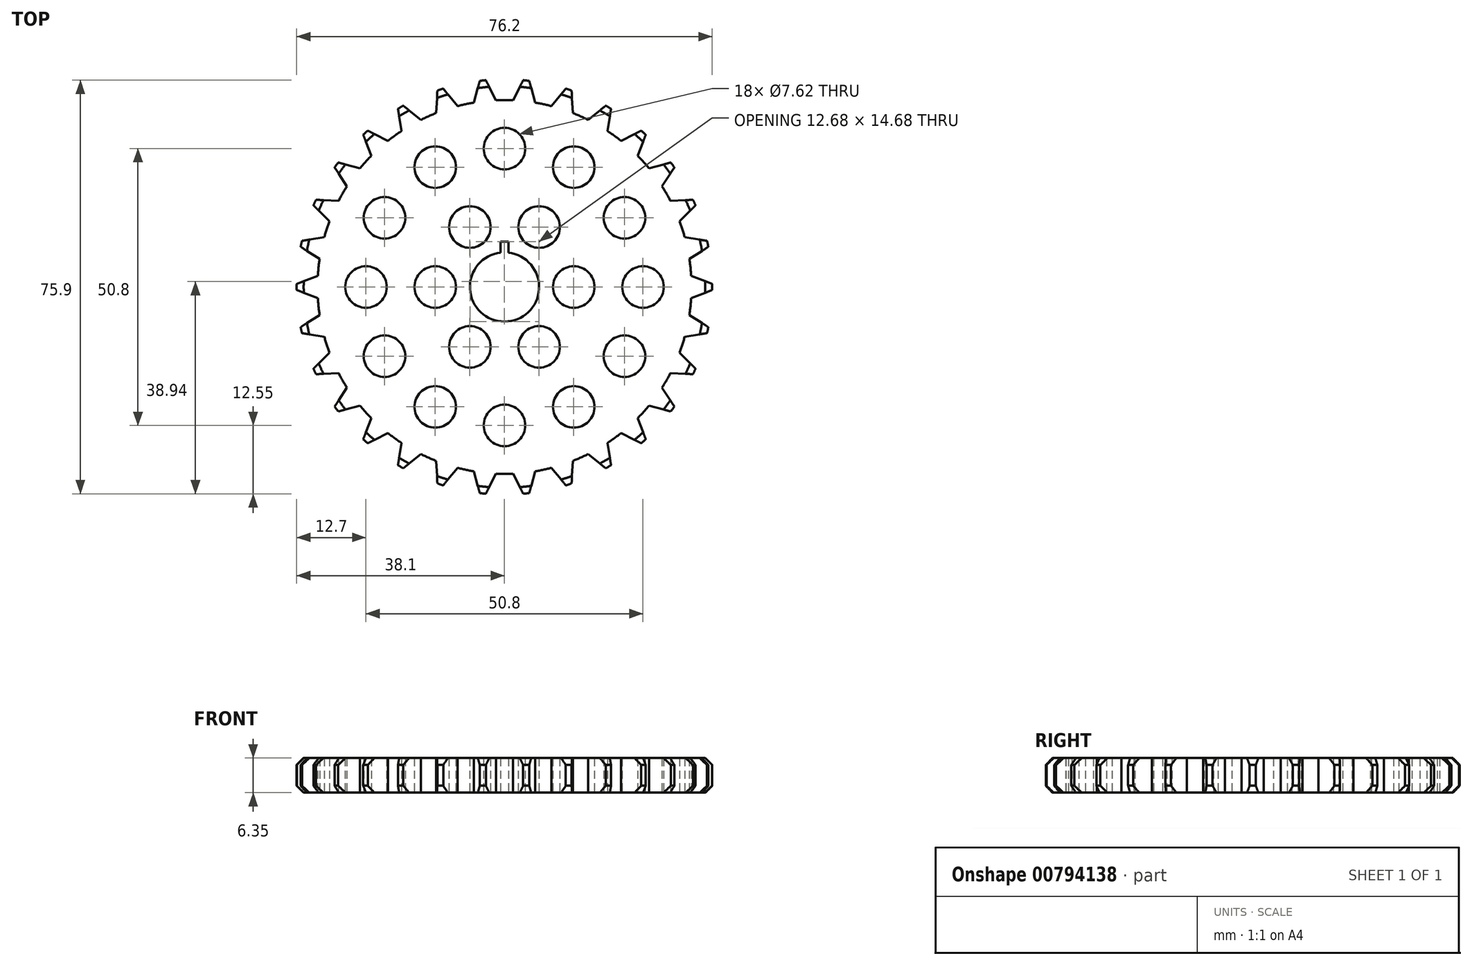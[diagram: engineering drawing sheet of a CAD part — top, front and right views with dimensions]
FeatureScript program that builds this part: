
annotation { "Feature Type Name" : "Feature", "Feature Type Description" : "" }
export const myFeature = defineFeature(function(context is Context, id is Id, definition is map)
    precondition{}
    {
        {
            var Q0;
            Q0=qCreatedBy(makeId("Top.planeOp"),FACE);
            var sketch = newSketch(context, id + "F0", { "sketchPlane" : qUnion([Q0])});
            skArc(sketch, "E0", {"start": v(12.3, 36.06) * mm, "mid": v(11.77, 36.24) * mm, "end": v(11.24, 36.4) * mm});
            skArc(sketch, "E1", {"start": v(-0.7, 6.31) * mm, "mid": v(0, -6.35) * mm, "end": v(0.7, 6.31) * mm});
            skArc(sketch, "E2", {"start": v(1.55, 34.26) * mm, "mid": v(0, 34.3) * mm, "end": v(-1.55, 34.26) * mm});
            skLineSegment(sketch, "E3", {"start": v(-1.55, 34.26) * mm, "end": v(-3.42, 37.95) * mm});
            skLineSegment(sketch, "E4.MirrorCS", {"start": v(1.55, 34.26) * mm, "end": v(3.42, 37.95) * mm});
            skArc(sketch, "E5.1.0", {"start": v(-5.61, 33.83) * mm, "mid": v(-7.13, 33.54) * mm, "end": v(-8.63, 33.19) * mm});
            skLineSegment(sketch, "E5.1.1", {"start": v(-8.63, 33.19) * mm, "end": v(-11.24, 36.4) * mm});
            skLineSegment(sketch, "E5.1.2", {"start": v(-5.61, 33.83) * mm, "end": v(-4.54, 37.83) * mm});
            skArc(sketch, "E5.2.0", {"start": v(-12.52, 31.92) * mm, "mid": v(-13.95, 31.33) * mm, "end": v(-15.34, 30.66) * mm});
            skLineSegment(sketch, "E5.2.1", {"start": v(-15.34, 30.66) * mm, "end": v(-18.56, 33.27) * mm});
            skLineSegment(sketch, "E5.2.2", {"start": v(-12.52, 31.92) * mm, "end": v(-12.3, 36.06) * mm});
            skArc(sketch, "E5.3.0", {"start": v(-18.88, 28.62) * mm, "mid": v(-20.16, 27.74) * mm, "end": v(-21.39, 26.8) * mm});
            skLineSegment(sketch, "E5.3.1", {"start": v(-21.39, 26.8) * mm, "end": v(-25.07, 28.69) * mm});
            skLineSegment(sketch, "E5.3.2", {"start": v(-18.88, 28.62) * mm, "end": v(-19.53, 32.71) * mm});
            skArc(sketch, "E5.4.0", {"start": v(-24.42, 24.07) * mm, "mid": v(-25.48, 22.94) * mm, "end": v(-26.5, 21.77) * mm});
            skLineSegment(sketch, "E5.4.1", {"start": v(-26.5, 21.77) * mm, "end": v(-30.5, 22.85) * mm});
            skLineSegment(sketch, "E5.4.2", {"start": v(-24.42, 24.07) * mm, "end": v(-25.9, 27.94) * mm});
            skArc(sketch, "E5.5.0", {"start": v(-28.9, 18.47) * mm, "mid": v(-29.7, 17.15) * mm, "end": v(-30.44, 15.79) * mm});
            skLineSegment(sketch, "E5.5.1", {"start": v(-30.44, 15.79) * mm, "end": v(-34.57, 16) * mm});
            skLineSegment(sketch, "E5.5.2", {"start": v(-28.9, 18.47) * mm, "end": v(-31.15, 21.94) * mm});
            skArc(sketch, "E5.6.0", {"start": v(-32.1, 12.06) * mm, "mid": v(-32.61, 10.6) * mm, "end": v(-33.06, 9.12) * mm});
            skLineSegment(sketch, "E5.6.1", {"start": v(-33.06, 9.12) * mm, "end": v(-37.15, 8.47) * mm});
            skLineSegment(sketch, "E5.6.2", {"start": v(-32.1, 12.06) * mm, "end": v(-35.03, 14.98) * mm});
            skArc(sketch, "E5.7.0", {"start": v(-33.9, 5.12) * mm, "mid": v(-34.1, 3.58) * mm, "end": v(-34.23, 2.04) * mm});
            skLineSegment(sketch, "E5.7.1", {"start": v(-34.23, 2.04) * mm, "end": v(-38.1, 0.56) * mm});
            skLineSegment(sketch, "E5.7.2", {"start": v(-33.9, 5.12) * mm, "end": v(-37.38, 7.37) * mm});
            skArc(sketch, "E5.8.0", {"start": v(-34.23, -2.04) * mm, "mid": v(-34.1, -3.58) * mm, "end": v(-33.9, -5.12) * mm});
            skLineSegment(sketch, "E5.8.1", {"start": v(-33.9, -5.12) * mm, "end": v(-37.38, -7.37) * mm});
            skLineSegment(sketch, "E5.8.2", {"start": v(-34.23, -2.04) * mm, "end": v(-38.1, -0.56) * mm});
            skArc(sketch, "E5.9.0", {"start": v(-33.06, -9.12) * mm, "mid": v(-32.61, -10.6) * mm, "end": v(-32.1, -12.06) * mm});
            skLineSegment(sketch, "E5.9.1", {"start": v(-32.1, -12.06) * mm, "end": v(-35.03, -14.98) * mm});
            skLineSegment(sketch, "E5.9.2", {"start": v(-33.06, -9.12) * mm, "end": v(-37.15, -8.47) * mm});
            skArc(sketch, "E5.10.0", {"start": v(-30.44, -15.79) * mm, "mid": v(-29.7, -17.14) * mm, "end": v(-28.9, -18.47) * mm});
            skLineSegment(sketch, "E5.10.1", {"start": v(-28.9, -18.47) * mm, "end": v(-31.15, -21.94) * mm});
            skLineSegment(sketch, "E5.10.2", {"start": v(-30.44, -15.79) * mm, "end": v(-34.57, -16) * mm});
            skArc(sketch, "E5.11.0", {"start": v(-26.5, -21.77) * mm, "mid": v(-25.48, -22.94) * mm, "end": v(-24.42, -24.07) * mm});
            skLineSegment(sketch, "E5.11.1", {"start": v(-24.42, -24.07) * mm, "end": v(-25.9, -27.94) * mm});
            skLineSegment(sketch, "E5.11.2", {"start": v(-26.5, -21.77) * mm, "end": v(-30.5, -22.85) * mm});
            skArc(sketch, "E5.12.0", {"start": v(-21.39, -26.8) * mm, "mid": v(-20.16, -27.74) * mm, "end": v(-18.88, -28.62) * mm});
            skLineSegment(sketch, "E5.12.1", {"start": v(-18.88, -28.62) * mm, "end": v(-19.53, -32.71) * mm});
            skLineSegment(sketch, "E5.12.2", {"start": v(-21.39, -26.8) * mm, "end": v(-25.07, -28.69) * mm});
            skArc(sketch, "E5.13.0", {"start": v(-15.34, -30.66) * mm, "mid": v(-13.95, -31.33) * mm, "end": v(-12.52, -31.92) * mm});
            skLineSegment(sketch, "E5.13.1", {"start": v(-12.52, -31.92) * mm, "end": v(-12.3, -36.06) * mm});
            skLineSegment(sketch, "E5.13.2", {"start": v(-15.34, -30.66) * mm, "end": v(-18.56, -33.27) * mm});
            skArc(sketch, "E5.14.0", {"start": v(-8.63, -33.19) * mm, "mid": v(-7.13, -33.54) * mm, "end": v(-5.61, -33.83) * mm});
            skLineSegment(sketch, "E5.14.1", {"start": v(-5.61, -33.83) * mm, "end": v(-4.54, -37.83) * mm});
            skLineSegment(sketch, "E5.14.2", {"start": v(-8.63, -33.19) * mm, "end": v(-11.24, -36.4) * mm});
            skArc(sketch, "E5.15.0", {"start": v(-1.55, -34.26) * mm, "mid": v(0, -34.3) * mm, "end": v(1.55, -34.26) * mm});
            skLineSegment(sketch, "E5.15.1", {"start": v(1.55, -34.26) * mm, "end": v(3.42, -37.95) * mm});
            skLineSegment(sketch, "E5.15.2", {"start": v(-1.55, -34.26) * mm, "end": v(-3.42, -37.95) * mm});
            skArc(sketch, "E5.16.0", {"start": v(5.61, -33.83) * mm, "mid": v(7.13, -33.54) * mm, "end": v(8.63, -33.19) * mm});
            skLineSegment(sketch, "E5.16.1", {"start": v(8.63, -33.19) * mm, "end": v(11.24, -36.4) * mm});
            skLineSegment(sketch, "E5.16.2", {"start": v(5.61, -33.83) * mm, "end": v(4.54, -37.83) * mm});
            skArc(sketch, "E5.17.0", {"start": v(12.52, -31.92) * mm, "mid": v(13.95, -31.33) * mm, "end": v(15.34, -30.66) * mm});
            skLineSegment(sketch, "E5.17.1", {"start": v(15.34, -30.66) * mm, "end": v(18.56, -33.27) * mm});
            skLineSegment(sketch, "E5.17.2", {"start": v(12.52, -31.92) * mm, "end": v(12.3, -36.06) * mm});
            skArc(sketch, "E5.18.0", {"start": v(18.88, -28.62) * mm, "mid": v(20.16, -27.74) * mm, "end": v(21.39, -26.8) * mm});
            skLineSegment(sketch, "E5.18.1", {"start": v(21.39, -26.8) * mm, "end": v(25.07, -28.69) * mm});
            skLineSegment(sketch, "E5.18.2", {"start": v(18.88, -28.62) * mm, "end": v(19.53, -32.71) * mm});
            skArc(sketch, "E5.19.0", {"start": v(24.42, -24.07) * mm, "mid": v(25.48, -22.94) * mm, "end": v(26.5, -21.77) * mm});
            skLineSegment(sketch, "E5.19.1", {"start": v(26.5, -21.77) * mm, "end": v(30.5, -22.85) * mm});
            skLineSegment(sketch, "E5.19.2", {"start": v(24.42, -24.07) * mm, "end": v(25.9, -27.94) * mm});
            skArc(sketch, "E5.20.0", {"start": v(28.9, -18.47) * mm, "mid": v(29.7, -17.15) * mm, "end": v(30.44, -15.79) * mm});
            skLineSegment(sketch, "E5.20.1", {"start": v(30.44, -15.79) * mm, "end": v(34.57, -16) * mm});
            skLineSegment(sketch, "E5.20.2", {"start": v(28.9, -18.47) * mm, "end": v(31.15, -21.94) * mm});
            skArc(sketch, "E5.21.0", {"start": v(32.1, -12.06) * mm, "mid": v(32.61, -10.6) * mm, "end": v(33.06, -9.12) * mm});
            skLineSegment(sketch, "E5.21.1", {"start": v(33.06, -9.12) * mm, "end": v(37.15, -8.47) * mm});
            skLineSegment(sketch, "E5.21.2", {"start": v(32.1, -12.06) * mm, "end": v(35.03, -14.98) * mm});
            skArc(sketch, "E5.22.0", {"start": v(33.9, -5.12) * mm, "mid": v(34.1, -3.58) * mm, "end": v(34.23, -2.04) * mm});
            skLineSegment(sketch, "E5.22.1", {"start": v(34.23, -2.04) * mm, "end": v(38.1, -0.56) * mm});
            skLineSegment(sketch, "E5.22.2", {"start": v(33.9, -5.12) * mm, "end": v(37.38, -7.37) * mm});
            skArc(sketch, "E5.23.0", {"start": v(34.23, 2.04) * mm, "mid": v(34.1, 3.58) * mm, "end": v(33.9, 5.12) * mm});
            skLineSegment(sketch, "E5.23.1", {"start": v(33.9, 5.12) * mm, "end": v(37.38, 7.37) * mm});
            skLineSegment(sketch, "E5.23.2", {"start": v(34.23, 2.04) * mm, "end": v(38.1, 0.56) * mm});
            skArc(sketch, "E5.24.0", {"start": v(33.06, 9.12) * mm, "mid": v(32.61, 10.6) * mm, "end": v(32.1, 12.06) * mm});
            skLineSegment(sketch, "E5.24.1", {"start": v(32.1, 12.06) * mm, "end": v(35.03, 14.98) * mm});
            skLineSegment(sketch, "E5.24.2", {"start": v(33.06, 9.12) * mm, "end": v(37.15, 8.47) * mm});
            skArc(sketch, "E5.25.0", {"start": v(30.44, 15.79) * mm, "mid": v(29.7, 17.14) * mm, "end": v(28.9, 18.47) * mm});
            skLineSegment(sketch, "E5.25.1", {"start": v(28.9, 18.47) * mm, "end": v(31.15, 21.94) * mm});
            skLineSegment(sketch, "E5.25.2", {"start": v(30.44, 15.79) * mm, "end": v(34.57, 16) * mm});
            skArc(sketch, "E5.26.0", {"start": v(26.5, 21.77) * mm, "mid": v(25.48, 22.94) * mm, "end": v(24.42, 24.07) * mm});
            skLineSegment(sketch, "E5.26.1", {"start": v(24.42, 24.07) * mm, "end": v(25.9, 27.94) * mm});
            skLineSegment(sketch, "E5.26.2", {"start": v(26.5, 21.77) * mm, "end": v(30.5, 22.85) * mm});
            skArc(sketch, "E5.27.0", {"start": v(21.39, 26.8) * mm, "mid": v(20.16, 27.74) * mm, "end": v(18.88, 28.62) * mm});
            skLineSegment(sketch, "E5.27.1", {"start": v(18.88, 28.62) * mm, "end": v(19.53, 32.71) * mm});
            skLineSegment(sketch, "E5.27.2", {"start": v(21.39, 26.8) * mm, "end": v(25.07, 28.69) * mm});
            skArc(sketch, "E5.28.0", {"start": v(15.34, 30.66) * mm, "mid": v(13.95, 31.33) * mm, "end": v(12.52, 31.92) * mm});
            skLineSegment(sketch, "E5.28.1", {"start": v(12.52, 31.92) * mm, "end": v(12.3, 36.06) * mm});
            skLineSegment(sketch, "E5.28.2", {"start": v(15.34, 30.66) * mm, "end": v(18.56, 33.27) * mm});
            skArc(sketch, "E5.29.0", {"start": v(8.63, 33.19) * mm, "mid": v(7.13, 33.54) * mm, "end": v(5.61, 33.83) * mm});
            skLineSegment(sketch, "E5.29.1", {"start": v(5.61, 33.83) * mm, "end": v(4.54, 37.83) * mm});
            skLineSegment(sketch, "E5.29.2", {"start": v(8.63, 33.19) * mm, "end": v(11.24, 36.4) * mm});
            skLineSegment(sketch, "E6", {"start": v(0.7, 6.31) * mm, "end": v(0.7, 8.33) * mm});
            skLineSegment(sketch, "E7", {"start": v(0.7, 8.33) * mm, "end": v(-0.7, 8.33) * mm});
            skLineSegment(sketch, "E8", {"start": v(-0.7, 8.33) * mm, "end": v(-0.7, 6.31) * mm});
            skArc(sketch, "E9.trimOffspring", {"start": v(4.54, 37.83) * mm, "mid": v(3.98, 37.9) * mm, "end": v(3.42, 37.95) * mm});
            skArc(sketch, "E10.trimOffspring", {"start": v(-3.42, 37.95) * mm, "mid": v(-3.98, 37.9) * mm, "end": v(-4.54, 37.83) * mm});
            skArc(sketch, "E11.trimOffspring", {"start": v(19.53, 32.71) * mm, "mid": v(19.05, 33) * mm, "end": v(18.56, 33.27) * mm});
            skArc(sketch, "E12.trimOffspring", {"start": v(-11.24, 36.4) * mm, "mid": v(-11.77, 36.24) * mm, "end": v(-12.3, 36.06) * mm});
            skArc(sketch, "E13.trimOffspring", {"start": v(31.15, 21.94) * mm, "mid": v(30.82, 22.4) * mm, "end": v(30.5, 22.85) * mm});
            skArc(sketch, "E14.trimOffspring", {"start": v(35.03, 14.98) * mm, "mid": v(34.8, 15.5) * mm, "end": v(34.57, 16) * mm});
            skArc(sketch, "E15.trimOffspring", {"start": v(37.38, 7.37) * mm, "mid": v(37.27, 7.92) * mm, "end": v(37.15, 8.47) * mm});
            skArc(sketch, "E16.trimOffspring", {"start": v(38.1, -0.56) * mm, "mid": v(38.1, 0) * mm, "end": v(38.1, 0.56) * mm});
            skArc(sketch, "E17.trimOffspring", {"start": v(37.15, -8.47) * mm, "mid": v(37.27, -7.92) * mm, "end": v(37.38, -7.37) * mm});
            skArc(sketch, "E18.trimOffspring", {"start": v(34.57, -16) * mm, "mid": v(34.8, -15.5) * mm, "end": v(35.03, -14.98) * mm});
            skArc(sketch, "E19.trimOffspring", {"start": v(30.5, -22.85) * mm, "mid": v(30.82, -22.4) * mm, "end": v(31.15, -21.94) * mm});
            skArc(sketch, "E20.trimOffspring", {"start": v(25.07, -28.69) * mm, "mid": v(25.5, -28.31) * mm, "end": v(25.9, -27.94) * mm});
            skArc(sketch, "E21.trimOffspring", {"start": v(18.56, -33.27) * mm, "mid": v(19.05, -33) * mm, "end": v(19.53, -32.71) * mm});
            skArc(sketch, "E22.trimOffspring", {"start": v(11.24, -36.4) * mm, "mid": v(11.77, -36.24) * mm, "end": v(12.3, -36.06) * mm});
            skArc(sketch, "E23.trimOffspring", {"start": v(3.42, -37.95) * mm, "mid": v(3.98, -37.9) * mm, "end": v(4.54, -37.83) * mm});
            skArc(sketch, "E24.trimOffspring", {"start": v(-4.54, -37.83) * mm, "mid": v(-3.98, -37.9) * mm, "end": v(-3.42, -37.95) * mm});
            skArc(sketch, "E25.trimOffspring", {"start": v(-12.3, -36.06) * mm, "mid": v(-11.77, -36.24) * mm, "end": v(-11.24, -36.4) * mm});
            skArc(sketch, "E26.trimOffspring", {"start": v(-19.53, -32.71) * mm, "mid": v(-19.05, -33) * mm, "end": v(-18.56, -33.27) * mm});
            skArc(sketch, "E27.trimOffspring", {"start": v(-25.9, -27.94) * mm, "mid": v(-25.5, -28.31) * mm, "end": v(-25.07, -28.69) * mm});
            skArc(sketch, "E28.trimOffspring", {"start": v(-31.15, -21.94) * mm, "mid": v(-30.82, -22.4) * mm, "end": v(-30.5, -22.85) * mm});
            skArc(sketch, "E29.trimOffspring", {"start": v(-35.03, -14.98) * mm, "mid": v(-34.8, -15.5) * mm, "end": v(-34.57, -16) * mm});
            skArc(sketch, "E30.trimOffspring", {"start": v(-37.38, -7.37) * mm, "mid": v(-37.27, -7.92) * mm, "end": v(-37.15, -8.47) * mm});
            skArc(sketch, "E31.trimOffspring", {"start": v(-38.1, 0.56) * mm, "mid": v(-38.1, 0) * mm, "end": v(-38.1, -0.56) * mm});
            skArc(sketch, "E32.trimOffspring", {"start": v(-37.15, 8.47) * mm, "mid": v(-37.27, 7.92) * mm, "end": v(-37.38, 7.37) * mm});
            skArc(sketch, "E33.trimOffspring", {"start": v(-34.57, 16) * mm, "mid": v(-34.8, 15.5) * mm, "end": v(-35.03, 14.98) * mm});
            skArc(sketch, "E34.trimOffspring", {"start": v(-30.5, 22.85) * mm, "mid": v(-30.82, 22.4) * mm, "end": v(-31.15, 21.94) * mm});
            skArc(sketch, "E35.trimOffspring", {"start": v(-25.07, 28.69) * mm, "mid": v(-25.5, 28.31) * mm, "end": v(-25.9, 27.94) * mm});
            skArc(sketch, "E36.trimOffspring", {"start": v(-18.56, 33.27) * mm, "mid": v(-19.05, 33) * mm, "end": v(-19.53, 32.71) * mm});
            skArc(sketch, "E37.trimOffspring", {"start": v(25.9, 27.94) * mm, "mid": v(25.5, 28.31) * mm, "end": v(25.07, 28.69) * mm});
            skCircle(sketch, "E38", {"center": v(0, 25.4) * mm, "radius": 3.81 * mm});
            skCircle(sketch, "E39.1.0", {"center": v(-12.7, 22) * mm, "radius": 3.81 * mm});
            skCircle(sketch, "E39.2.0", {"center": v(-22, 12.7) * mm, "radius": 3.81 * mm});
            skCircle(sketch, "E40.1.3.0", {"center": v(-25.4, 0) * mm, "radius": 3.81 * mm});
            skCircle(sketch, "E40.1.4.0", {"center": v(-22, -12.7) * mm, "radius": 3.81 * mm});
            skCircle(sketch, "E40.1.5.0", {"center": v(-12.7, -22) * mm, "radius": 3.81 * mm});
            skCircle(sketch, "E41", {"center": v(-12.7, 0) * mm, "radius": 3.81 * mm});
            skCircle(sketch, "E42.1.0", {"center": v(-6.35, -11) * mm, "radius": 3.81 * mm});
            skCircle(sketch, "E42.2.0", {"center": v(6.35, -11) * mm, "radius": 3.81 * mm});
            skCircle(sketch, "E43.1.3.0", {"center": v(12.7, 0) * mm, "radius": 3.81 * mm});
            skCircle(sketch, "E43.1.4.0", {"center": v(6.35, 11) * mm, "radius": 3.81 * mm});
            skCircle(sketch, "E43.1.5.0", {"center": v(-6.35, 11) * mm, "radius": 3.81 * mm});
            skCircle(sketch, "E44.1.6.0", {"center": v(0, -25.4) * mm, "radius": 3.81 * mm});
            skCircle(sketch, "E44.1.7.0", {"center": v(12.7, -22) * mm, "radius": 3.81 * mm});
            skCircle(sketch, "E44.1.8.0", {"center": v(22, -12.7) * mm, "radius": 3.81 * mm});
            skCircle(sketch, "E44.1.9.0", {"center": v(25.4, 0) * mm, "radius": 3.81 * mm});
            skCircle(sketch, "E44.1.10.0", {"center": v(22, 12.7) * mm, "radius": 3.81 * mm});
            skCircle(sketch, "E44.1.11.0", {"center": v(12.7, 22) * mm, "radius": 3.81 * mm});
            skSolve(sketch);
        }
        {
            var Q0;
            Q0=makeQuery(id+"F0.imprint","IMPRINT",FACE,{"disambiguationData":[TD([[makeQuery(id+"F0.imprint","IMPRINT",EDGE,{"derivedFrom":sQuery(id+"F0.wireOp",EDGE,"E1")}),-1.0]])]});
            var sketch = newSketch(context, id + "F1", { "sketchPlane" : qUnion([Q0])});
            skSolve(sketch);
        }
        {
            var Q0;
            Q0 = qSketchRegion(id + "F1", true);
            var Q1;
            Q1=makeQuery(id+"F0.imprint","IMPRINT",FACE,{"disambiguationData":[TD([[makeQuery(id+"F0.imprint","IMPRINT",EDGE,{"derivedFrom":sQuery(id+"F0.wireOp",EDGE,"E2")}),1.0]])]});
            extrude(context, id + "F2", {"entities" : qUnion([Q0, Q1]), "depth" : 6.35 * mm, "offsetDistance" : 25.4 * mm});
        }
        {
            var Q0;
            Q0=makeQuery(id+"F2.opExtrude","CAP_EDGE",EDGE,{"disambiguationData":[OSD([sQuery(id+"F0.wireOp",EDGE,"E9.trimOffspring")])],"isStart":true});
            var Q1;
            Q1=makeQuery(id+"F2.opExtrude","CAP_EDGE",EDGE,{"disambiguationData":[OSD([sQuery(id+"F0.wireOp",EDGE,"E10.trimOffspring")])],"isStart":true});
            var Q2;
            Q2=makeQuery(id+"F2.opExtrude","CAP_EDGE",EDGE,{"disambiguationData":[OSD([sQuery(id+"F0.wireOp",EDGE,"E12.trimOffspring")])],"isStart":true});
            var Q3;
            Q3=makeQuery(id+"F2.opExtrude","CAP_EDGE",EDGE,{"disambiguationData":[OSD([sQuery(id+"F0.wireOp",EDGE,"E36.trimOffspring")])],"isStart":true});
            var Q4;
            Q4=makeQuery(id+"F2.opExtrude","CAP_EDGE",EDGE,{"disambiguationData":[OSD([sQuery(id+"F0.wireOp",EDGE,"E35.trimOffspring")])],"isStart":true});
            var Q5;
            Q5=makeQuery(id+"F2.opExtrude","CAP_EDGE",EDGE,{"disambiguationData":[OSD([sQuery(id+"F0.wireOp",EDGE,"E34.trimOffspring")])],"isStart":true});
            var Q6;
            Q6=makeQuery(id+"F2.opExtrude","CAP_EDGE",EDGE,{"disambiguationData":[OSD([sQuery(id+"F0.wireOp",EDGE,"E33.trimOffspring")])],"isStart":true});
            var Q7;
            Q7=makeQuery(id+"F2.opExtrude","CAP_EDGE",EDGE,{"disambiguationData":[OSD([sQuery(id+"F0.wireOp",EDGE,"E32.trimOffspring")])],"isStart":true});
            var Q8;
            Q8=makeQuery(id+"F2.opExtrude","CAP_EDGE",EDGE,{"disambiguationData":[OSD([sQuery(id+"F0.wireOp",EDGE,"E31.trimOffspring")])],"isStart":true});
            var Q9;
            Q9=makeQuery(id+"F2.opExtrude","CAP_EDGE",EDGE,{"disambiguationData":[OSD([sQuery(id+"F0.wireOp",EDGE,"E30.trimOffspring")])],"isStart":true});
            var Q10;
            Q10=makeQuery(id+"F2.opExtrude","CAP_EDGE",EDGE,{"disambiguationData":[OSD([sQuery(id+"F0.wireOp",EDGE,"E29.trimOffspring")])],"isStart":true});
            var Q11;
            Q11=makeQuery(id+"F2.opExtrude","CAP_EDGE",EDGE,{"disambiguationData":[OSD([sQuery(id+"F0.wireOp",EDGE,"E28.trimOffspring")])],"isStart":true});
            var Q12;
            Q12=makeQuery(id+"F2.opExtrude","CAP_EDGE",EDGE,{"disambiguationData":[OSD([sQuery(id+"F0.wireOp",EDGE,"E27.trimOffspring")])],"isStart":true});
            var Q13;
            Q13=makeQuery(id+"F2.opExtrude","CAP_EDGE",EDGE,{"disambiguationData":[OSD([sQuery(id+"F0.wireOp",EDGE,"E26.trimOffspring")])],"isStart":true});
            var Q14;
            Q14=makeQuery(id+"F2.opExtrude","CAP_EDGE",EDGE,{"disambiguationData":[OSD([sQuery(id+"F0.wireOp",EDGE,"E25.trimOffspring")])],"isStart":true});
            var Q15;
            Q15=makeQuery(id+"F2.opExtrude","CAP_EDGE",EDGE,{"disambiguationData":[OSD([sQuery(id+"F0.wireOp",EDGE,"E24.trimOffspring")])],"isStart":true});
            var Q16;
            Q16=makeQuery(id+"F2.opExtrude","CAP_EDGE",EDGE,{"disambiguationData":[OSD([sQuery(id+"F0.wireOp",EDGE,"E23.trimOffspring")])],"isStart":true});
            var Q17;
            Q17=makeQuery(id+"F2.opExtrude","CAP_EDGE",EDGE,{"disambiguationData":[OSD([sQuery(id+"F0.wireOp",EDGE,"E22.trimOffspring")])],"isStart":true});
            var Q18;
            Q18=makeQuery(id+"F2.opExtrude","CAP_EDGE",EDGE,{"disambiguationData":[OSD([sQuery(id+"F0.wireOp",EDGE,"E21.trimOffspring")])],"isStart":true});
            var Q19;
            Q19=makeQuery(id+"F2.opExtrude","CAP_EDGE",EDGE,{"disambiguationData":[OSD([sQuery(id+"F0.wireOp",EDGE,"E20.trimOffspring")])],"isStart":true});
            var Q20;
            Q20=makeQuery(id+"F2.opExtrude","CAP_EDGE",EDGE,{"disambiguationData":[OSD([sQuery(id+"F0.wireOp",EDGE,"E19.trimOffspring")])],"isStart":true});
            var Q21;
            Q21=makeQuery(id+"F2.opExtrude","CAP_EDGE",EDGE,{"disambiguationData":[OSD([sQuery(id+"F0.wireOp",EDGE,"E18.trimOffspring")])],"isStart":true});
            var Q22;
            Q22=makeQuery(id+"F2.opExtrude","CAP_EDGE",EDGE,{"disambiguationData":[OSD([sQuery(id+"F0.wireOp",EDGE,"E17.trimOffspring")])],"isStart":true});
            var Q23;
            Q23=makeQuery(id+"F2.opExtrude","CAP_EDGE",EDGE,{"disambiguationData":[OSD([sQuery(id+"F0.wireOp",EDGE,"E16.trimOffspring")])],"isStart":true});
            var Q24;
            Q24=makeQuery(id+"F2.opExtrude","CAP_EDGE",EDGE,{"disambiguationData":[OSD([sQuery(id+"F0.wireOp",EDGE,"E15.trimOffspring")])],"isStart":true});
            var Q25;
            Q25=makeQuery(id+"F2.opExtrude","CAP_EDGE",EDGE,{"disambiguationData":[OSD([sQuery(id+"F0.wireOp",EDGE,"E14.trimOffspring")])],"isStart":true});
            var Q26;
            Q26=makeQuery(id+"F2.opExtrude","CAP_EDGE",EDGE,{"disambiguationData":[OSD([sQuery(id+"F0.wireOp",EDGE,"E13.trimOffspring")])],"isStart":true});
            var Q27;
            Q27=makeQuery(id+"F2.opExtrude","CAP_EDGE",EDGE,{"disambiguationData":[OSD([sQuery(id+"F0.wireOp",EDGE,"E37.trimOffspring")])],"isStart":true});
            var Q28;
            Q28=makeQuery(id+"F2.opExtrude","CAP_EDGE",EDGE,{"disambiguationData":[OSD([sQuery(id+"F0.wireOp",EDGE,"E11.trimOffspring")])],"isStart":true});
            var Q29;
            Q29=makeQuery(id+"F2.opExtrude","CAP_EDGE",EDGE,{"disambiguationData":[OSD([sQuery(id+"F0.wireOp",EDGE,"E0")])],"isStart":true});
            var Q30;
            Q30=makeQuery(id+"F2.opExtrude","CAP_EDGE",EDGE,{"disambiguationData":[OSD([sQuery(id+"F0.wireOp",EDGE,"E12.trimOffspring")])],"isStart":false});
            var Q31;
            Q31=makeQuery(id+"F2.opExtrude","CAP_EDGE",EDGE,{"disambiguationData":[OSD([sQuery(id+"F0.wireOp",EDGE,"E10.trimOffspring")])],"isStart":false});
            var Q32;
            Q32=makeQuery(id+"F2.opExtrude","CAP_EDGE",EDGE,{"disambiguationData":[OSD([sQuery(id+"F0.wireOp",EDGE,"E9.trimOffspring")])],"isStart":false});
            var Q33;
            Q33=makeQuery(id+"F2.opExtrude","CAP_EDGE",EDGE,{"disambiguationData":[OSD([sQuery(id+"F0.wireOp",EDGE,"E0")])],"isStart":false});
            var Q34;
            Q34=makeQuery(id+"F2.opExtrude","CAP_EDGE",EDGE,{"disambiguationData":[OSD([sQuery(id+"F0.wireOp",EDGE,"E11.trimOffspring")])],"isStart":false});
            var Q35;
            Q35=makeQuery(id+"F2.opExtrude","CAP_EDGE",EDGE,{"disambiguationData":[OSD([sQuery(id+"F0.wireOp",EDGE,"E37.trimOffspring")])],"isStart":false});
            var Q36;
            Q36=makeQuery(id+"F2.opExtrude","CAP_EDGE",EDGE,{"disambiguationData":[OSD([sQuery(id+"F0.wireOp",EDGE,"E13.trimOffspring")])],"isStart":false});
            var Q37;
            Q37=makeQuery(id+"F2.opExtrude","CAP_EDGE",EDGE,{"disambiguationData":[OSD([sQuery(id+"F0.wireOp",EDGE,"E14.trimOffspring")])],"isStart":false});
            var Q38;
            Q38=makeQuery(id+"F2.opExtrude","CAP_EDGE",EDGE,{"disambiguationData":[OSD([sQuery(id+"F0.wireOp",EDGE,"E15.trimOffspring")])],"isStart":false});
            var Q39;
            Q39=makeQuery(id+"F2.opExtrude","CAP_EDGE",EDGE,{"disambiguationData":[OSD([sQuery(id+"F0.wireOp",EDGE,"E17.trimOffspring")])],"isStart":false});
            var Q40;
            Q40=makeQuery(id+"F2.opExtrude","CAP_EDGE",EDGE,{"disambiguationData":[OSD([sQuery(id+"F0.wireOp",EDGE,"E16.trimOffspring")])],"isStart":false});
            var Q41;
            Q41=makeQuery(id+"F2.opExtrude","CAP_EDGE",EDGE,{"disambiguationData":[OSD([sQuery(id+"F0.wireOp",EDGE,"E18.trimOffspring")])],"isStart":false});
            var Q42;
            Q42=makeQuery(id+"F2.opExtrude","CAP_EDGE",EDGE,{"disambiguationData":[OSD([sQuery(id+"F0.wireOp",EDGE,"E19.trimOffspring")])],"isStart":false});
            var Q43;
            Q43=makeQuery(id+"F2.opExtrude","CAP_EDGE",EDGE,{"disambiguationData":[OSD([sQuery(id+"F0.wireOp",EDGE,"E20.trimOffspring")])],"isStart":false});
            var Q44;
            Q44=makeQuery(id+"F2.opExtrude","CAP_EDGE",EDGE,{"disambiguationData":[OSD([sQuery(id+"F0.wireOp",EDGE,"E21.trimOffspring")])],"isStart":false});
            var Q45;
            Q45=makeQuery(id+"F2.opExtrude","CAP_EDGE",EDGE,{"disambiguationData":[OSD([sQuery(id+"F0.wireOp",EDGE,"E22.trimOffspring")])],"isStart":false});
            var Q46;
            Q46=makeQuery(id+"F2.opExtrude","CAP_EDGE",EDGE,{"disambiguationData":[OSD([sQuery(id+"F0.wireOp",EDGE,"E23.trimOffspring")])],"isStart":false});
            var Q47;
            Q47=makeQuery(id+"F2.opExtrude","CAP_EDGE",EDGE,{"disambiguationData":[OSD([sQuery(id+"F0.wireOp",EDGE,"E24.trimOffspring")])],"isStart":false});
            var Q48;
            Q48=makeQuery(id+"F2.opExtrude","CAP_EDGE",EDGE,{"disambiguationData":[OSD([sQuery(id+"F0.wireOp",EDGE,"E26.trimOffspring")])],"isStart":false});
            var Q49;
            Q49=makeQuery(id+"F2.opExtrude","CAP_EDGE",EDGE,{"disambiguationData":[OSD([sQuery(id+"F0.wireOp",EDGE,"E25.trimOffspring")])],"isStart":false});
            var Q50;
            Q50=makeQuery(id+"F2.opExtrude","CAP_EDGE",EDGE,{"disambiguationData":[OSD([sQuery(id+"F0.wireOp",EDGE,"E27.trimOffspring")])],"isStart":false});
            var Q51;
            Q51=makeQuery(id+"F2.opExtrude","CAP_EDGE",EDGE,{"disambiguationData":[OSD([sQuery(id+"F0.wireOp",EDGE,"E28.trimOffspring")])],"isStart":false});
            var Q52;
            Q52=makeQuery(id+"F2.opExtrude","CAP_EDGE",EDGE,{"disambiguationData":[OSD([sQuery(id+"F0.wireOp",EDGE,"E29.trimOffspring")])],"isStart":false});
            var Q53;
            Q53=makeQuery(id+"F2.opExtrude","CAP_EDGE",EDGE,{"disambiguationData":[OSD([sQuery(id+"F0.wireOp",EDGE,"E30.trimOffspring")])],"isStart":false});
            var Q54;
            Q54=makeQuery(id+"F2.opExtrude","CAP_EDGE",EDGE,{"disambiguationData":[OSD([sQuery(id+"F0.wireOp",EDGE,"E31.trimOffspring")])],"isStart":false});
            var Q55;
            Q55=makeQuery(id+"F2.opExtrude","CAP_EDGE",EDGE,{"disambiguationData":[OSD([sQuery(id+"F0.wireOp",EDGE,"E32.trimOffspring")])],"isStart":false});
            var Q56;
            Q56=makeQuery(id+"F2.opExtrude","CAP_EDGE",EDGE,{"disambiguationData":[OSD([sQuery(id+"F0.wireOp",EDGE,"E33.trimOffspring")])],"isStart":false});
            var Q57;
            Q57=makeQuery(id+"F2.opExtrude","CAP_EDGE",EDGE,{"disambiguationData":[OSD([sQuery(id+"F0.wireOp",EDGE,"E34.trimOffspring")])],"isStart":false});
            var Q58;
            Q58=makeQuery(id+"F2.opExtrude","CAP_EDGE",EDGE,{"disambiguationData":[OSD([sQuery(id+"F0.wireOp",EDGE,"E35.trimOffspring")])],"isStart":false});
            var Q59;
            Q59=makeQuery(id+"F2.opExtrude","CAP_EDGE",EDGE,{"disambiguationData":[OSD([sQuery(id+"F0.wireOp",EDGE,"E36.trimOffspring")])],"isStart":false});
            chamfer(context, id + "F3", {"entities" : qUnion([Q0, Q1, Q2, Q3, Q4, Q5, Q6, Q7, Q8, Q9, Q10, Q11, Q12, Q13, Q14, Q15, Q16, Q17, Q18, Q19, Q20, Q21, Q22, Q23, Q24, Q25, Q26, Q27, Q28, Q29, Q30, Q31, Q32, Q33, Q34, Q35, Q36, Q37, Q38, Q39, Q40, Q41, Q42, Q43, Q44, Q45, Q46, Q47, Q48, Q49, Q50, Q51, Q52, Q53, Q54, Q55, Q56, Q57, Q58, Q59]), "width" : 1.27 * mm, "tangentPropagation" : true});
        }
    });
